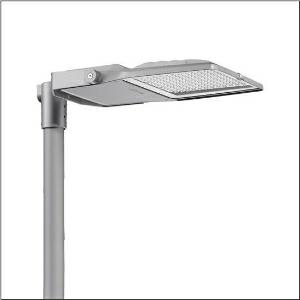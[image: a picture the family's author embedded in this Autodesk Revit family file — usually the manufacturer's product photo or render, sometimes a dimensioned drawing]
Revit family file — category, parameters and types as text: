
# Revit family: floodlight_fl_21_iq_midi___pl43_5xa7782f2a3a_db1b
name_source: partatom
category: Lighting Fixtures
units: mm (PartAtom-declared; Revit-internal decimal feet)

## family parameters
Cut with Voids When Loaded = No
Host = Face
Light Source = No
Part Type = Normal
Room Calculation Point = No
Round Connector Dimension = Use Diameter
Shared = No

## types (1)
- --- (1 x LED, 36680 lm, 270.2 W, 3000K)
    Apparent Load = 270 VA
    CIE Flux Codes = 27 78 99 100 100
    Color Rendering = 70
    Color Temperature = 3000K
    Default Elevation = 1800 mm
    Description = Floodlight FL 21 iQ midi, floodlight, primary light control with lens, of PMMA, primary optical cover: protective disc, of toughened safety glass, transparent, light distribution: PL43, light emission: direct distribution, installation type: surface-mounted, lamps: LED, High Power LED, rated values: 36.680lm | 270,2W | 135,8lm/W (begin service life); end service life: 36.680lm | 286,6W; at 50% lumin. flux: 18.340lm | 117,4W | 156,2lm/W, colour temperature: 3000K, colour rendering: CRI > 70, light colour: 730, light setting 1 begin service life: 100% | 36.680lm | 270,2W | 135,8lm/W | 3.000K, light setting 1 end service life: 286,6W, further light settings possible, control: optimised constant luminous flux control (CLO 2.0), Desk-Remote (wireless, voltage-free reading and setting of iQ features in the workshop via application-optimized NFC function/RFID function), Smart-Wire, Night-Set, Temp-Guard, Auto-Match, Street-Remote, pre-setting: linear dimming characteristic, with terminal, 6-pole, mains connection: 220..240V, AC, 50/60Hz, luminaire housing, of diecast aluminium, powder-coated, SITECO metallic grey (DB 702S), corrosivity category C5 mid according to DIN EN ISO 12944suitable for swimming poolschlorine-resistant, sealing non-destructively replaceable, please order mast flange separately, mast bracket, of steel, galvanised, powder-coated, SITECO metallic grey (DB 702S), protection rating (complete): IP66, insulation class (complete): insulation class II (safety insulation), certification: CE, ENEC, VDE, protection symbol: D, impact resistance: IK08, permissible operating ambient temperature: -40..+40°C, permissible operating ambient temperature for outdoor applications: -40..+50°C, standard: DIN EN 12944, LABS conformity tested according to VDMA 24364:2018-05, packaging unit: 1 piece

Light Distribution: PL43
    Height = 76 mm
    Lamp = 1 x LED
    Lamp Light Flux = 36680 lm
    Lamp Power = 270.2 W
    Lamp count = 1
    Length = 657 mm
    Luminous efficacy = 136 lm/W
    Manufacturer = Siteco
    ModVariant = No
    Model = 5XA7782F2A3A
    Number of Poles = 1
    OnlyDefault = Yes
    Power Factor = 1
    Product Name = Floodlight FL 21 iQ midi | PL43
    Product group = floodlight | pylon annexe
    ProductGroupID = 6201
    Protection Class = Protection class II
    Protection Degree = IP 66
    RLX_Detail_Level = 1
    RLX_Emergency_Light_Flux = 0 lm
    RLX_Emergency_Type = 0
    RLX_Emergency_Type_DB = No
    RlxData = <blob elided: 154001 chars, md5=6cd022e3>
    Socket = socket
    Standby Power = 0 W
    System Light Flux = 36680 lm
    System Power = 270 W
    Type Comments = factory setting: luminous flux: 100 % | dim-lin: 254 | 620 mA
    Type Image = l_1007123.jpg
    URL = http://relux.com
    VarID = @adj_104643
    Voltage = 0 V
    Weight = 0.00 kg
    Width = 442 mm

## geometry (parser evidence)
native form markers: Blend x4, Sweep x11
no freeform markers — native parametric forms only
